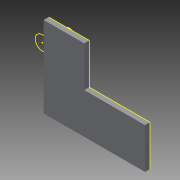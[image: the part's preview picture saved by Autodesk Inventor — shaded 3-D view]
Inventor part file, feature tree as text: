
AUTODESK INVENTOR PART (.ipt)
format: ipt  version: 2013 (Build 170138000, 138)  size: 84,992 bytes
history: native  units: in
note: dims shown in document units (in); Inventor stores cm internally (conversion verified against a paired STEP export)
features: reference x6, sketch x3, extrude x2
ambient origin geometry x8: Origin, YZ Plane, XZ Plane, XY Plane, X Axis, Y Axis, Z Axis, Center Point
bodies: Solid1 (feature_tree)
feature tree (11):
  extrude  "Extrusion1"  Depth=1.0in
  sketch  "Sketch2"  dims[d3=1.0in d4=1.5in]
  sketch  "Sketch3"  dims[d5=0.125in d6=0.0in d7=1.0in d8=0.0in]
  extrude  "Extrusion2"  Depth=1.5in
  sketch  "Sketch1"  dims[d0=2.0in d2=1.0in]
  reference  "Reference1"
  reference  "Reference2"
  reference  "Reference3"
  reference  "Reference4"
  reference  "Reference5"
  reference  "Reference6"
